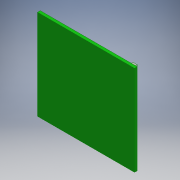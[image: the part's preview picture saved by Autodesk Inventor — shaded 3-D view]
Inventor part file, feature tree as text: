
AUTODESK INVENTOR PART (.ipt)
format: ipt  version: 2019 (Build 230136000, 136)  size: 113,152 bytes
history: native  units: mm
features: extrude x2, sketch x2, other x1
ambient origin geometry x8: Origin, YZ Plane, XZ Plane, XY Plane, X Axis, Y Axis, Z Axis, Center Point
bodies: Solide1 (feature_tree)
feature tree (5):
  other  "PCB Wifi"
  extrude  "Extrusion1"  Depth=56.0mm
  extrude  "Extrusion2"  Depth=28.0mm
  sketch  "Esquisse1"
  sketch  "Esquisse2"
